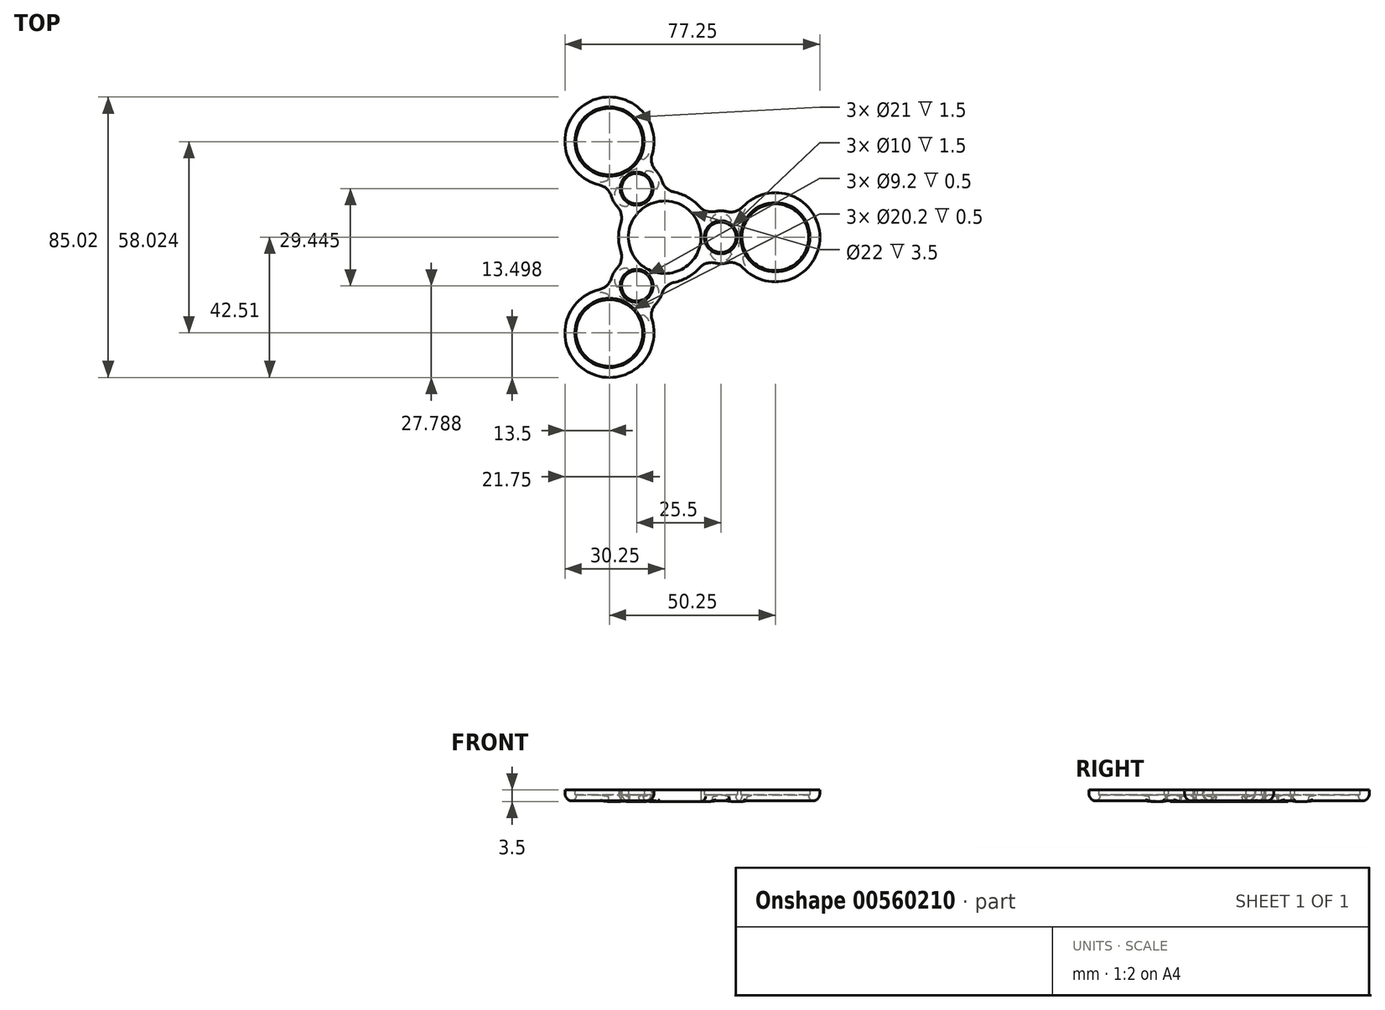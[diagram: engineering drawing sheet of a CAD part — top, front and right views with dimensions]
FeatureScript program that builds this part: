
annotation { "Feature Type Name" : "Feature", "Feature Type Description" : "" }
export const myFeature = defineFeature(function(context is Context, id is Id, definition is map)
    precondition{}
    {
        {
            var Q0;
            Q0=qCreatedBy(makeId("Top.planeOp"),FACE);
            var sketch = newSketch(context, id + "F0", { "sketchPlane" : qUnion([Q0])});
            skCircle(sketch, "E0", {"center": v(0, 0) * mm, "radius": 11 * mm});
            skCircle(sketch, "E1", {"center": v(17, 0) * mm, "radius": 5 * mm});
            skCircle(sketch, "E2", {"center": v(33.5, 0) * mm, "radius": 10.5 * mm});
            skArc(sketch, "E3.0", {"start": v(23.65, -9.23) * mm, "mid": v(47, 0) * mm, "end": v(23.65, 9.23) * mm});
            skArc(sketch, "E4.0", {"start": v(15.24, -7.8) * mm, "mid": v(17.05, -8) * mm, "end": v(18.85, -7.78) * mm});
            skArc(sketch, "E5.0", {"start": v(-13.3, 4.35) * mm, "mid": v(-14, 0) * mm, "end": v(-13.3, -4.35) * mm});
            skCircle(sketch, "E6", {"center": v(-16.75, 29.01) * mm, "radius": 10.5 * mm});
            skCircle(sketch, "E7", {"center": v(-8.5, -14.72) * mm, "radius": 5 * mm});
            skCircle(sketch, "E8", {"center": v(-16.75, -29.01) * mm, "radius": 10.5 * mm});
            skCircle(sketch, "E9", {"center": v(-8.5, 14.72) * mm, "radius": 5 * mm});
            skArc(sketch, "E10.0", {"start": v(-3.83, 25.1) * mm, "mid": v(-23.5, 40.7) * mm, "end": v(-19.82, 15.87) * mm});
            skArc(sketch, "E11.0", {"start": v(-16.16, 12.43) * mm, "mid": v(-15.45, 10.76) * mm, "end": v(-14.38, 9.3) * mm});
            skArc(sketch, "E12.0", {"start": v(-14.38, -9.3) * mm, "mid": v(-15.45, -10.76) * mm, "end": v(-16.16, -12.43) * mm});
            skArc(sketch, "E13.0", {"start": v(-19.82, -15.87) * mm, "mid": v(-23.5, -40.7) * mm, "end": v(-3.83, -25.1) * mm});
            skArc(sketch, "E14.trimOffspring", {"start": v(-0.86, 17.1) * mm, "mid": v(-1.6, 18.76) * mm, "end": v(-2.68, 20.21) * mm});
            skArc(sketch, "E15.trimOffspring", {"start": v(2.88, -13.7) * mm, "mid": v(7, -12.12) * mm, "end": v(10.42, -9.35) * mm});
            skArc(sketch, "E16.trimOffspring", {"start": v(-2.68, -20.21) * mm, "mid": v(-1.6, -18.76) * mm, "end": v(-0.86, -17.1) * mm});
            skArc(sketch, "E17.trimOffspring", {"start": v(10.42, 9.35) * mm, "mid": v(7, 12.12) * mm, "end": v(2.88, 13.7) * mm});
            skArc(sketch, "E18.trimOffspring", {"start": v(18.85, 7.78) * mm, "mid": v(17.05, 8) * mm, "end": v(15.24, 7.8) * mm});
            skPoint(sketch, "E19.visualSharp", {"position": v(21.67, 6.5) * mm});
            skArc(sketch, "E19.filletArc", {"start": v(18.85, 7.78) * mm, "mid": v(21.44, 7.86) * mm, "end": v(23.65, 9.23) * mm});
            skPoint(sketch, "E20.visualSharp", {"position": v(12.38, 6.53) * mm});
            skArc(sketch, "E20.filletArc", {"start": v(10.42, 9.35) * mm, "mid": v(12.62, 7.92) * mm, "end": v(15.24, 7.8) * mm});
            skPoint(sketch, "E21.visualSharp", {"position": v(-0.53, 13.99) * mm});
            skArc(sketch, "E21.filletArc", {"start": v(-0.86, 17.1) * mm, "mid": v(0.55, 14.9) * mm, "end": v(2.88, 13.7) * mm});
            skPoint(sketch, "E22.visualSharp", {"position": v(-5.2, 22.01) * mm});
            skArc(sketch, "E22.filletArc", {"start": v(-3.83, 25.1) * mm, "mid": v(-3.91, 22.5) * mm, "end": v(-2.68, 20.21) * mm});
            skPoint(sketch, "E23.visualSharp", {"position": v(-16.46, 15.51) * mm});
            skArc(sketch, "E23.filletArc", {"start": v(-16.16, 12.43) * mm, "mid": v(-17.53, 14.64) * mm, "end": v(-19.82, 15.87) * mm});
            skPoint(sketch, "E24.visualSharp", {"position": v(-11.85, 7.46) * mm});
            skArc(sketch, "E24.filletArc", {"start": v(-13.3, 4.35) * mm, "mid": v(-13.17, 6.97) * mm, "end": v(-14.38, 9.3) * mm});
            skPoint(sketch, "E25.visualSharp", {"position": v(-0.53, -13.99) * mm});
            skArc(sketch, "E25.filletArc", {"start": v(2.88, -13.7) * mm, "mid": v(0.55, -14.9) * mm, "end": v(-0.86, -17.1) * mm});
            skPoint(sketch, "E26.visualSharp", {"position": v(-5.2, -22.01) * mm});
            skArc(sketch, "E26.filletArc", {"start": v(-2.68, -20.21) * mm, "mid": v(-3.91, -22.5) * mm, "end": v(-3.83, -25.1) * mm});
            skPoint(sketch, "E27.visualSharp", {"position": v(-11.85, -7.46) * mm});
            skArc(sketch, "E27.filletArc", {"start": v(-14.38, -9.3) * mm, "mid": v(-13.17, -6.97) * mm, "end": v(-13.3, -4.35) * mm});
            skPoint(sketch, "E28.visualSharp", {"position": v(-16.46, -15.51) * mm});
            skArc(sketch, "E28.filletArc", {"start": v(-19.82, -15.87) * mm, "mid": v(-17.53, -14.64) * mm, "end": v(-16.16, -12.43) * mm});
            skPoint(sketch, "E29.visualSharp", {"position": v(21.67, -6.5) * mm});
            skArc(sketch, "E29.filletArc", {"start": v(23.65, -9.23) * mm, "mid": v(21.44, -7.86) * mm, "end": v(18.85, -7.78) * mm});
            skPoint(sketch, "E30.visualSharp", {"position": v(12.38, -6.53) * mm});
            skArc(sketch, "E30.filletArc", {"start": v(15.24, -7.8) * mm, "mid": v(12.62, -7.92) * mm, "end": v(10.42, -9.35) * mm});
            skCircle(sketch, "E31.0", {"center": v(-16.75, 29.01) * mm, "radius": 10.1 * mm});
            skCircle(sketch, "E32.0", {"center": v(-8.5, 14.72) * mm, "radius": 4.6 * mm});
            skCircle(sketch, "E33.0", {"center": v(-16.75, -29.01) * mm, "radius": 10.1 * mm});
            skCircle(sketch, "E34.0", {"center": v(-8.5, -14.72) * mm, "radius": 4.6 * mm});
            skCircle(sketch, "E35.0", {"center": v(17, 0) * mm, "radius": 4.6 * mm});
            skCircle(sketch, "E36.0", {"center": v(33.5, 0) * mm, "radius": 10.1 * mm});
            skSolve(sketch);
        }
        {
            var Q0;
            Q0=makeQuery(id+"F0.imprint","IMPRINT",FACE,{"disambiguationData":[TD([[makeQuery(id+"F0.imprint","IMPRINT",EDGE,{"derivedFrom":sQuery(id+"F0.wireOp",EDGE,"E0")}),-1.0]])]});
            extrude(context, id + "F1", {"entities" : qUnion([Q0]), "depth" : 3.5 * mm, "offsetDistance" : 25 * mm});
        }
        {
            var Q0;
            Q0=makeQuery(id+"F0.imprint","IMPRINT",FACE,{"disambiguationData":[TD([[makeQuery(id+"F0.imprint","IMPRINT",EDGE,{"derivedFrom":sQuery(id+"F0.wireOp",EDGE,"E9")}),1.0]])]});
            var Q1;
            Q1=makeQuery(id+"F0.imprint","IMPRINT",FACE,{"disambiguationData":[TD([[makeQuery(id+"F0.imprint","IMPRINT",EDGE,{"derivedFrom":sQuery(id+"F0.wireOp",EDGE,"E6")}),1.0]])]});
            var Q2;
            Q2=makeQuery(id+"F0.imprint","IMPRINT",FACE,{"disambiguationData":[TD([[makeQuery(id+"F0.imprint","IMPRINT",EDGE,{"derivedFrom":sQuery(id+"F0.wireOp",EDGE,"E7")}),1.0]])]});
            var Q3;
            Q3=makeQuery(id+"F0.imprint","IMPRINT",FACE,{"disambiguationData":[TD([[makeQuery(id+"F0.imprint","IMPRINT",EDGE,{"derivedFrom":sQuery(id+"F0.wireOp",EDGE,"E8")}),1.0]])]});
            var Q4;
            Q4=makeQuery(id+"F0.imprint","IMPRINT",FACE,{"disambiguationData":[TD([[makeQuery(id+"F0.imprint","IMPRINT",EDGE,{"derivedFrom":sQuery(id+"F0.wireOp",EDGE,"E1")}),1.0]])]});
            var Q5;
            Q5=makeQuery(id+"F0.imprint","IMPRINT",FACE,{"disambiguationData":[TD([[makeQuery(id+"F0.imprint","IMPRINT",EDGE,{"derivedFrom":sQuery(id+"F0.wireOp",EDGE,"E2")}),1.0]])]});
            extrude(context, id + "F2", {"entities" : qUnion([Q0, Q1, Q2, Q3, Q4, Q5]), "operationType" : NewBodyOperationType.ADD, "depth" : 2 * mm, "offsetDistance" : 25 * mm});
        }
        {
            var Q0;
            Q0=makeQuery(id+"F1.opExtrude","CAP_EDGE",EDGE,{"disambiguationData":[OSD([sQuery(id+"F0.wireOp",EDGE,"E10.0")])],"isStart":true});
            fillet(context, id + "F3", {"entities" : qUnion([Q0]), "radius" : 2.5 * mm, "tangentPropagation" : true, "allowEdgeOverflow" : false});
        }
        {
            var Q0;
            Q0=makeQuery(id+"F2.opExtrude","CAP_EDGE",EDGE,{"disambiguationData":[OSD([sQuery(id+"F0.wireOp",EDGE,"E34.0")])],"isStart":true});
            var Q1;
            Q1=makeQuery(id+"F2.opExtrude","CAP_EDGE",EDGE,{"disambiguationData":[OSD([sQuery(id+"F0.wireOp",EDGE,"E33.0")])],"isStart":true});
            var Q2;
            Q2=makeQuery(id+"F2.opExtrude","CAP_EDGE",EDGE,{"disambiguationData":[OSD([sQuery(id+"F0.wireOp",EDGE,"E32.0")])],"isStart":true});
            var Q3;
            Q3=makeQuery(id+"F2.opExtrude","CAP_EDGE",EDGE,{"disambiguationData":[OSD([sQuery(id+"F0.wireOp",EDGE,"E31.0")])],"isStart":true});
            var Q4;
            Q4=makeQuery(id+"F2.opExtrude","CAP_EDGE",EDGE,{"disambiguationData":[OSD([sQuery(id+"F0.wireOp",EDGE,"E36.0")])],"isStart":true});
            var Q5;
            Q5=makeQuery(id+"F2.opExtrude","CAP_EDGE",EDGE,{"disambiguationData":[OSD([sQuery(id+"F0.wireOp",EDGE,"E35.0")])],"isStart":true});
            fillet(context, id + "F4", {"entities" : qUnion([Q0, Q1, Q2, Q3, Q4, Q5]), "radius" : 1.5 * mm, "tangentPropagation" : true, "allowEdgeOverflow" : false});
        }
    });
